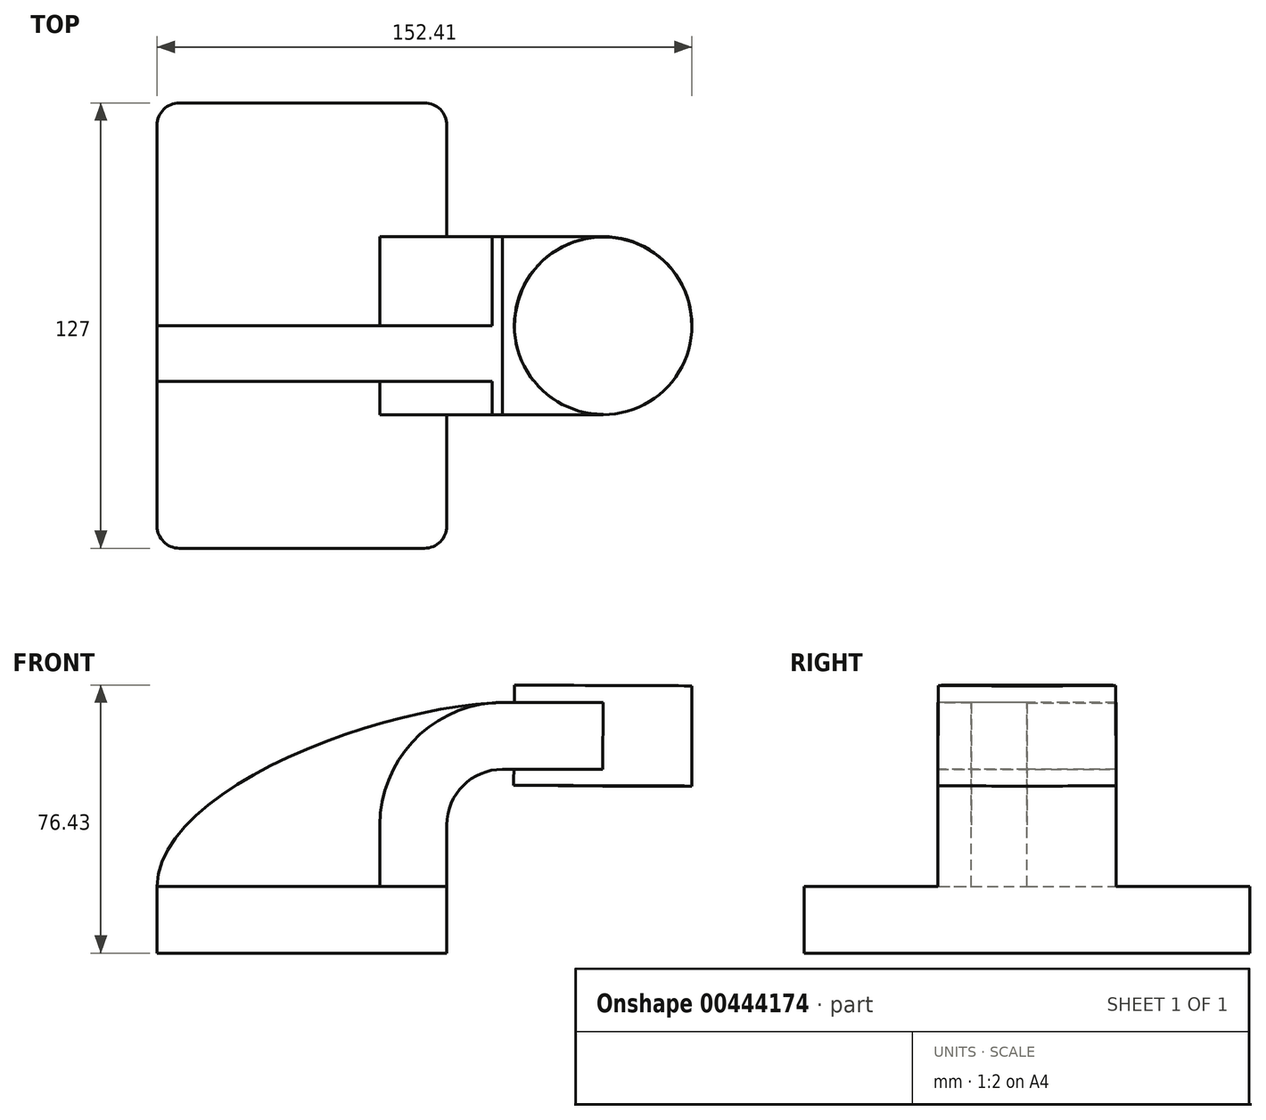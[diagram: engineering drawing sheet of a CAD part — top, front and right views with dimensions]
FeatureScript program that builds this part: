
annotation { "Feature Type Name" : "Feature", "Feature Type Description" : "" }
export const myFeature = defineFeature(function(context is Context, id is Id, definition is map)
    precondition{}
    {
        {
            var Q0;
            Q0=qCreatedBy(makeId("Front.planeOp"),FACE);
            var sketch = newSketch(context, id + "F0", { "sketchPlane" : qUnion([Q0])});
            skLineSegment(sketch, "E0.bottom", {"start": v(-41.27, -9.53) * mm, "end": v(41.28, -9.53) * mm});
            skLineSegment(sketch, "E0.top", {"start": v(-41.28, 9.53) * mm, "end": v(41.28, 9.53) * mm});
            skLineSegment(sketch, "E0.left", {"start": v(-41.28, -9.53) * mm, "end": v(-41.28, 9.53) * mm});
            skLineSegment(sketch, "E0.right", {"start": v(41.28, -9.53) * mm, "end": v(41.28, 9.52) * mm});
            skPoint(sketch, "E0.middle", {"position": v(0, 0) * mm});
            skLineSegment(sketch, "E1.bottom", {"start": v(60.32, 38.1) * mm, "end": v(111.12, 38.1) * mm});
            skLineSegment(sketch, "E1.top", {"start": v(60.32, 66.67) * mm, "end": v(111.12, 66.67) * mm});
            skLineSegment(sketch, "E1.left", {"start": v(60.32, 38.1) * mm, "end": v(60.32, 66.67) * mm});
            skLineSegment(sketch, "E1.right", {"start": v(111.12, 38.1) * mm, "end": v(111.12, 66.67) * mm});
            skPoint(sketch, "E1.middle", {"position": v(85.72, 52.39) * mm});
            skLineSegment(sketch, "E2", {"start": v(41.28, 9.52) * mm, "end": v(41.28, 27) * mm});
            skArc(sketch, "E3", {"start": v(41.27, 27) * mm, "mid": v(45.92, 38.23) * mm, "end": v(57.15, 42.88) * mm});
            skLineSegment(sketch, "E4", {"start": v(57.15, 42.88) * mm, "end": v(85.85, 42.88) * mm});
            skLineSegment(sketch, "E5.0", {"start": v(57.15, 61.93) * mm, "end": v(85.85, 61.93) * mm});
            skArc(sketch, "E5.1", {"start": v(22.22, 27) * mm, "mid": v(32.45, 51.7) * mm, "end": v(57.15, 61.93) * mm});
            skLineSegment(sketch, "E5.2", {"start": v(22.22, 9.52) * mm, "end": v(22.22, 27) * mm});
            skLineSegment(sketch, "E6", {"start": v(85.72, 38.1) * mm, "end": v(85.85, 66.67) * mm});
            skFitSpline(sketch, "E7", {"points": [v(-41.28, 9.53) * mm, v(57.15, 61.93) * mm], "startDerivative": vector(1.4, 83.88) * mm, "endDerivative": vector(103.43, 2.59) * mm});
            skSolve(sketch);
        }
        {
            var Q0;
            Q0=makeQuery(id+"F0.imprint","IMPRINT",FACE,{"disambiguationData":[TD([[makeQuery(id+"F0.imprint","IMPRINT",EDGE,{"derivedFrom":sQuery(id+"F0.wireOp",EDGE,"E0.bottom")}),1.0]])]});
            extrude(context, id + "F1", {"entities" : qUnion([Q0]), "endBound" : BoundingType.SYMMETRIC, "depth" : 127 * mm});
        }
        {
            var Q0;
            {var subQ1=sQuery(id+"F0.wireOp",EDGE,"E2");Q0=makeQuery(id+"F0.imprint","IMPRINT",FACE,{"disambiguationData":[TD([[makeQuery(id+"F0.imprint","IMPRINT",EDGE,{"derivedFrom":subQ1}),1.0]])]});}
            var Q1;
            {var subQ0=sQuery(id+"F0.wireOp",EDGE,"E4");var subQ1=sQuery(id+"F0.wireOp",EDGE,"E1.left");var subQ2=makeQuery(id+"F0.imprint","INTERSECT",VERTEX,{"derivedFrom":[subQ1,subQ0]});Q1=makeQuery(id+"F0.imprint","IMPRINT",FACE,{"disambiguationData":[TD([[makeQuery(id+"F0.imprint","IMPRINT",EDGE,{"disambiguationData":[TD([[subQ2,-1.0]])],"derivedFrom":subQ1}),-1.0]])]});}
            extrude(context, id + "F2", {"entities" : qUnion([Q0, Q1]), "operationType" : NewBodyOperationType.ADD, "endBound" : BoundingType.SYMMETRIC, "depth" : 50.8 * mm});
        }
        {
            var Q0;
            {var subQ3=sQuery(id+"F0.wireOp",EDGE,"E5.2");Q0=makeQuery(id+"F0.imprint","IMPRINT",FACE,{"disambiguationData":[TD([[makeQuery(id+"F0.imprint","IMPRINT",EDGE,{"derivedFrom":subQ3}),1.0]])]});}
            extrude(context, id + "F3", {"entities" : qUnion([Q0]), "operationType" : NewBodyOperationType.ADD, "depth" : 15.88 * mm});
        }
        {
            var Q0;
            {var subQ4=sQuery(id+"F0.wireOp",EDGE,"E1.right");Q0=makeQuery(id+"F0.imprint","IMPRINT",FACE,{"disambiguationData":[TD([[makeQuery(id+"F0.imprint","IMPRINT",EDGE,{"derivedFrom":subQ4}),1.0]])]});}
            var Q1;
            Q1=sQuery(id+"F0.wireOp",EDGE,"E6");
            revolve(context, id + "F4", {"operationType" : NewBodyOperationType.ADD, "entities" : qUnion([Q0]), "axis" : qUnion([Q1]), "revolveType" : RevolveType.FULL});
        }
        {
            var Q0;
            Q0=makeQuery(id+"F1.opExtrude","CAP_EDGE",EDGE,{"disambiguationData":[OSD([sQuery(id+"F0.wireOp",EDGE,"E0.right")])],"isStart":false});
            var Q1;
            Q1=makeQuery(id+"F1.opExtrude","CAP_EDGE",EDGE,{"disambiguationData":[OSD([sQuery(id+"F0.wireOp",EDGE,"E0.left")])],"isStart":false});
            var Q2;
            Q2=makeQuery(id+"F1.opExtrude","CAP_EDGE",EDGE,{"disambiguationData":[OSD([sQuery(id+"F0.wireOp",EDGE,"E0.right")])],"isStart":true});
            var Q3;
            Q3=makeQuery(id+"F1.opExtrude","CAP_EDGE",EDGE,{"disambiguationData":[OSD([sQuery(id+"F0.wireOp",EDGE,"E0.left")])],"isStart":true});
            fillet(context, id + "F5", {"entities" : qUnion([Q0, Q1, Q2, Q3]), "radius" : 6.35 * mm, "tangentPropagation" : true, "allowEdgeOverflow" : false});
        }
    });
